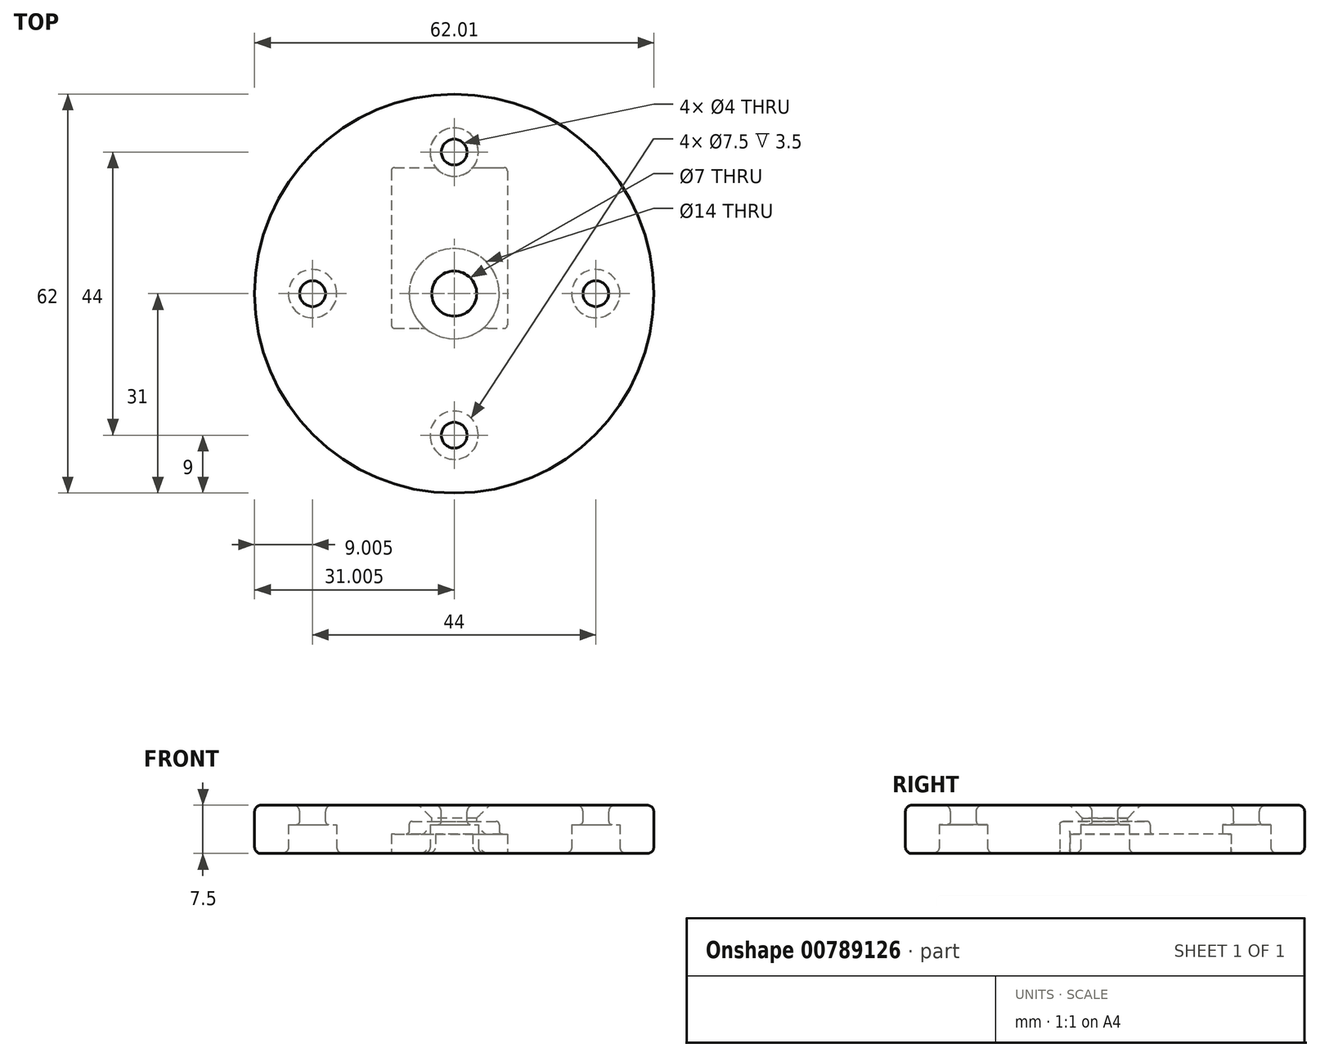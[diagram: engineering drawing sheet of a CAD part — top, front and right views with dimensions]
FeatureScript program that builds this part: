
annotation { "Feature Type Name" : "Feature", "Feature Type Description" : "" }
export const myFeature = defineFeature(function(context is Context, id is Id, definition is map)
    precondition{}
    {
        {
            var Q0;
            Q0=qCreatedBy(makeId("Top.planeOp"),FACE);
            var sketch = newSketch(context, id + "F0", { "sketchPlane" : qUnion([Q0])});
            skLineSegment(sketch, "E0", {"start": v(0, 0) * mm, "end": v(44.88, 0) * mm, "construction": true});
            skLineSegment(sketch, "E1", {"start": v(0, 0) * mm, "end": v(-44.88, 0) * mm, "construction": true});
            skCircle(sketch, "E2", {"center": v(-44.88, 0) * mm, "radius": 3.5 * mm});
            skCircle(sketch, "E3", {"center": v(44.88, 0) * mm, "radius": 3.5 * mm});
            skCircle(sketch, "E4", {"center": v(-44.88, 0) * mm, "radius": 31 * mm});
            skCircle(sketch, "E5", {"center": v(-44.88, 0) * mm, "radius": 22 * mm, "construction": true});
            skPoint(sketch, "E6", {"position": v(-44.88, 22) * mm});
            skPoint(sketch, "E7", {"position": v(-66.87, 0) * mm});
            skPoint(sketch, "E8", {"position": v(-44.88, -22) * mm});
            skPoint(sketch, "E9", {"position": v(-22.88, 0) * mm});
            skCircle(sketch, "E10", {"center": v(-44.88, 22) * mm, "radius": 2 * mm});
            skCircle(sketch, "E11", {"center": v(-66.87, 0) * mm, "radius": 2 * mm});
            skCircle(sketch, "E12", {"center": v(-44.88, -22) * mm, "radius": 2 * mm});
            skCircle(sketch, "E13", {"center": v(-22.88, 0) * mm, "radius": 2 * mm});
            skSolve(sketch);
        }
        {
            var Q0;
            Q0=makeQuery(id+"F0.imprint","IMPRINT",FACE,{"disambiguationData":[TD([[makeQuery(id+"F0.imprint","IMPRINT",EDGE,{"derivedFrom":sQuery(id+"F0.wireOp",EDGE,"E10")}),-1.0]])]});
            var Q1;
            Q1=makeQuery(id+"F0.imprint","IMPRINT",FACE,{"disambiguationData":[TD([[makeQuery(id+"F0.imprint","IMPRINT",EDGE,{"derivedFrom":sQuery(id+"F0.wireOp",EDGE,"E13")}),-1.0]])]});
            extrude(context, id + "F1", {"entities" : qUnion([Q0, Q1]), "oppositeDirection" : true, "depth" : 7.5 * mm});
        }
        {
            var Q0;
            Q0=makeQuery(id+"F1.opExtrude","CAP_FACE",FACE,{"disambiguationData":[OSD([sQuery(id+"F0.wireOp",EDGE,"UtSojWLK-Axtw-wVSr-lVTc-6Qd8189fFZQg"),sQuery(id+"F0.wireOp",EDGE,"E2"),sQuery(id+"F0.wireOp",EDGE,"E3"),sQuery(id+"F0.wireOp",EDGE,"FokHbOu8-fEOc-FsWC-vcUf-28nsGhh90SPb"),sQuery(id+"F0.wireOp",EDGE,"ryVjNOqA-lODm-GvTz-wMqV-SOG7XD1yc1lL"),sQuery(id+"F0.wireOp",EDGE,"E4"),sQuery(id+"F0.wireOp",EDGE,"E10"),sQuery(id+"F0.wireOp",EDGE,"E11"),sQuery(id+"F0.wireOp",EDGE,"E12"),sQuery(id+"F0.wireOp",EDGE,"E13")])],"isStart":false});
            var sketch = newSketch(context, id + "F2", { "sketchPlane" : qUnion([Q0])});
            skCircle(sketch, "E14", {"center": v(-44.88, 22) * mm, "radius": 3.75 * mm});
            skCircle(sketch, "E15", {"center": v(-22.88, 0) * mm, "radius": 3.75 * mm});
            skCircle(sketch, "E16", {"center": v(-44.88, -22) * mm, "radius": 3.75 * mm});
            skCircle(sketch, "E17", {"center": v(-66.87, 0) * mm, "radius": 3.75 * mm});
            skSolve(sketch);
        }
        {
            var Q0;
            Q0=qSketchRegion(id+"F2",true);
            extrude(context, id + "F3", {"entities" : qUnion([Q0]), "operationType" : NewBodyOperationType.REMOVE, "oppositeDirection" : true, "depth" : 4.5 * mm});
        }
        {
            var Q0;
            Q0=makeQuery(id+"F1.opExtrude","CAP_EDGE",EDGE,{"disambiguationData":[OSD([sQuery(id+"F0.wireOp",EDGE,"E2")])],"isStart":true});
            chamfer(context, id + "F4", {"entities" : qUnion([Q0]), "width" : 2 * mm, "tangentPropagation" : true});
        }
        {
            var Q0;
            Q0=makeQuery(id+"FrYEty1sIvLQoTp_1.opExtrude","CAP_FACE",FACE,{"disambiguationData":[OSD([sQuery(id+"F0.wireOp",EDGE,"S2UXTJ5L-PYoN-hTdS-oQlw-xzllwW9uqox5"),sQuery(id+"F0.wireOp",EDGE,"E2")])],"isStart":false});
            var Q1;
            Q1=makeQuery(id+"F1.opExtrude","CAP_FACE",FACE,{"disambiguationData":[OSD([sQuery(id+"F0.wireOp",EDGE,"S2UXTJ5L-PYoN-hTdS-oQlw-xzllwW9uqox5"),sQuery(id+"F0.wireOp",EDGE,"UtSojWLK-Axtw-wVSr-lVTc-6Qd8189fFZQg"),sQuery(id+"F0.wireOp",EDGE,"E2"),sQuery(id+"F0.wireOp",EDGE,"E3"),sQuery(id+"F0.wireOp",EDGE,"FokHbOu8-fEOc-FsWC-vcUf-28nsGhh90SPb"),sQuery(id+"F0.wireOp",EDGE,"ryVjNOqA-lODm-GvTz-wMqV-SOG7XD1yc1lL")])],"isStart":true});
            var Q2;
            Q2=makeQuery(id+"FrYEty1sIvLQoTp_1.opExtrude","CAP_FACE",FACE,{"disambiguationData":[OSD([sQuery(id+"F0.wireOp",EDGE,"UtSojWLK-Axtw-wVSr-lVTc-6Qd8189fFZQg"),sQuery(id+"F0.wireOp",EDGE,"E3")])],"isStart":false});
            var Q3;
            Q3=makeQuery(id+"F1.opExtrude","CAP_FACE",FACE,{"disambiguationData":[OSD([sQuery(id+"F0.wireOp",EDGE,"S2UXTJ5L-PYoN-hTdS-oQlw-xzllwW9uqox5"),sQuery(id+"F0.wireOp",EDGE,"UtSojWLK-Axtw-wVSr-lVTc-6Qd8189fFZQg"),sQuery(id+"F0.wireOp",EDGE,"E2"),sQuery(id+"F0.wireOp",EDGE,"E3"),sQuery(id+"F0.wireOp",EDGE,"FokHbOu8-fEOc-FsWC-vcUf-28nsGhh90SPb"),sQuery(id+"F0.wireOp",EDGE,"ryVjNOqA-lODm-GvTz-wMqV-SOG7XD1yc1lL")])],"isStart":false});
            fillet(context, id + "F5", {"entities" : qUnion([Q0, Q1, Q2, Q3]), "radius" : 1 * mm, "tangentPropagation" : true, "allowEdgeOverflow" : false});
        }
        {
            var Q0;
            Q0=makeQuery(id+"F1.opExtrude","SWEPT_FACE",FACE,{"disambiguationData":[OSD([sQuery(id+"F0.wireOp",EDGE,"E11")])]});
            var Q1;
            Q1=makeQuery(id+"F1.opExtrude","SWEPT_FACE",FACE,{"disambiguationData":[OSD([sQuery(id+"F0.wireOp",EDGE,"E12")])]});
            var Q2;
            Q2=makeQuery(id+"F1.opExtrude","SWEPT_FACE",FACE,{"disambiguationData":[OSD([sQuery(id+"F0.wireOp",EDGE,"E13")])]});
            var Q3;
            Q3=makeQuery(id+"F1.opExtrude","SWEPT_FACE",FACE,{"disambiguationData":[OSD([sQuery(id+"F0.wireOp",EDGE,"E10")])]});
            fillet(context, id + "F6", {"entities" : qUnion([Q0, Q1, Q2, Q3]), "radius" : .5 * mm, "tangentPropagation" : true, "allowEdgeOverflow" : false});
        }
        {
            var Q0;
            Q0=makeQuery(id+"F1.opExtrude","CAP_FACE",FACE,{"disambiguationData":[OSD([sQuery(id+"F0.wireOp",EDGE,"E2"),sQuery(id+"F0.wireOp",EDGE,"E4"),sQuery(id+"F0.wireOp",EDGE,"E10"),sQuery(id+"F0.wireOp",EDGE,"E11"),sQuery(id+"F0.wireOp",EDGE,"E12"),sQuery(id+"F0.wireOp",EDGE,"E13")])],"isStart":false});
            var sketch = newSketch(context, id + "F7", { "sketchPlane" : qUnion([Q0])});
            skLineSegment(sketch, "E18.bottom", {"start": v(-54.62, -19.6) * mm, "end": v(-36.62, -19.6) * mm});
            skLineSegment(sketch, "E18.top", {"start": v(-54.62, 5.4) * mm, "end": v(-36.62, 5.4) * mm});
            skLineSegment(sketch, "E18.left", {"start": v(-54.62, -19.6) * mm, "end": v(-54.62, 5.4) * mm});
            skLineSegment(sketch, "E18.right", {"start": v(-36.62, -19.6) * mm, "end": v(-36.62, 5.4) * mm});
            skSolve(sketch);
        }
        {
            var Q0;
            Q0=qSketchRegion(id+"F7",true);
            extrude(context, id + "F8", {"entities" : qUnion([Q0]), "operationType" : NewBodyOperationType.REMOVE, "oppositeDirection" : true, "depth" : 3 * mm});
        }
        {
            var Q0;
            Q0=makeQuery(id+"F8.boolean.opBoolean","COPY",FACE,{"derivedFrom":makeQuery(id+"F8.opExtrude","CAP_FACE",FACE,{"disambiguationData":[OSD([sQuery(id+"F7.wireOp",EDGE,"E18.bottom"),sQuery(id+"F7.wireOp",EDGE,"E18.top"),sQuery(id+"F7.wireOp",EDGE,"E18.left"),sQuery(id+"F7.wireOp",EDGE,"E18.right")])],"isStart":false})});
            var sketch = newSketch(context, id + "F9", { "sketchPlane" : qUnion([Q0])});
            skCircle(sketch, "E19", {"center": v(-44.88, 0) * mm, "radius": 7 * mm});
            skSolve(sketch);
        }
        {
            var Q0;
            Q0=qSketchRegion(id+"F9",true);
            extrude(context, id + "F10", {"entities" : qUnion([Q0]), "operationType" : NewBodyOperationType.REMOVE, "oppositeDirection" : true, "depth" : 2 * mm, "hasSecondDirection" : true, "secondDirectionOppositeDirection" : false, "secondDirectionDepth" : 25 * mm});
        }
        {
            var Q0;
            Q0=makeQuery(id+"F8.boolean.opBoolean","COPY",EDGE,{"derivedFrom":makeQuery(id+"F8.opExtrude","SWEPT_EDGE",EDGE,{"disambiguationData":[OSD([sQuery(id+"F7.wireOp",EDGE,"E18.top"),sQuery(id+"F7.wireOp",EDGE,"E18.left")])]})});
            var Q1;
            Q1=makeQuery(id+"F8.boolean.opBoolean","COPY",EDGE,{"derivedFrom":makeQuery(id+"F8.opExtrude","SWEPT_EDGE",EDGE,{"disambiguationData":[OSD([sQuery(id+"F7.wireOp",EDGE,"E18.top"),sQuery(id+"F7.wireOp",EDGE,"E18.right")])]})});
            var Q2;
            Q2=makeQuery(id+"F8.boolean.opBoolean","COPY",EDGE,{"derivedFrom":makeQuery(id+"F8.opExtrude","SWEPT_EDGE",EDGE,{"disambiguationData":[OSD([sQuery(id+"F7.wireOp",EDGE,"E18.bottom"),sQuery(id+"F7.wireOp",EDGE,"E18.right")])]})});
            var Q3;
            Q3=makeQuery(id+"F8.boolean.opBoolean","COPY",EDGE,{"derivedFrom":makeQuery(id+"F8.opExtrude","SWEPT_EDGE",EDGE,{"disambiguationData":[OSD([sQuery(id+"F7.wireOp",EDGE,"E18.bottom"),sQuery(id+"F7.wireOp",EDGE,"E18.left")])]})});
            var Q4;
            Q4=makeQuery(id+"F8.boolean.opBoolean","INTERSECT",EDGE,{"derivedFrom":[makeQuery(id+"F1.opExtrude","SWEPT_FACE",FACE,{"disambiguationData":[OSD([sQuery(id+"F0.wireOp",EDGE,"E2")])]}),makeQuery(id+"F8.opExtrude","CAP_FACE",FACE,{"disambiguationData":[OSD([sQuery(id+"F7.wireOp",EDGE,"E18.bottom"),sQuery(id+"F7.wireOp",EDGE,"E18.top"),sQuery(id+"F7.wireOp",EDGE,"E18.left"),sQuery(id+"F7.wireOp",EDGE,"E18.right")])],"isStart":false})]});
            var Q5;
            Q5=makeQuery(id+"F8.boolean.opBoolean","COPY",EDGE,{"derivedFrom":makeQuery(id+"F8.opExtrude","CAP_EDGE",EDGE,{"disambiguationData":[OSD([sQuery(id+"F7.wireOp",EDGE,"E18.bottom")])],"isStart":true})});
            var Q6;
            Q6=makeQuery(id+"F10.boolean.opBoolean","COPY",FACE,{"derivedFrom":makeQuery(id+"F10.opExtrude","SWEPT_FACE",FACE,{"disambiguationData":[OSD([sQuery(id+"F9.wireOp",EDGE,"E19")])]})});
            fillet(context, id + "F11", {"entities" : qUnion([Q0, Q1, Q2, Q3, Q4, Q5, Q6]), "radius" : .5 * mm, "tangentPropagation" : true, "allowEdgeOverflow" : false});
        }
    });
